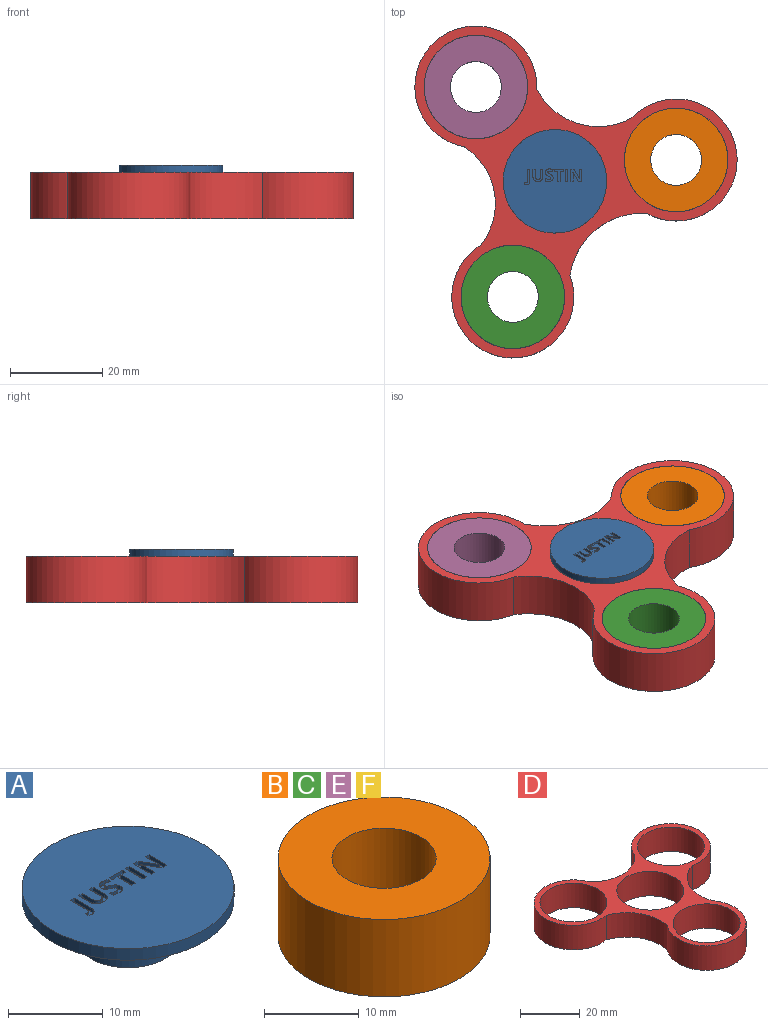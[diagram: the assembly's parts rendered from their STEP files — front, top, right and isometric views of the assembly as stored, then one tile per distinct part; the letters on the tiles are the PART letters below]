
ASSEMBLY  parts=6 mates=5
PART A: 90 faces, bbox 22.4x22.4x6.5 mm
  f0: plane 22.4x22.4mm, normal (0,0,1), area 378.7mm2, adj f3,f5,f6,f7,f8,f9,f10,f11
  f1: cylinder r=5.5mm len=11mm, axis (0,0,-1), area 172.8mm2, adj f2,f4
  f2: plane 11x11mm, normal (0,0,-1), area 95mm2, adj f1
  f3: cylinder r=11.2mm len=22.4mm, axis (0,0,-1), area 105.6mm2, adj f0,f4
  f4: plane 22.4x22.4mm, normal (0,0,-1), area 299mm2, adj f1,f3
  f5: plane 0.71x0.5mm, normal (0,1,0), area 0.4mm2, adj f0,f6,f18,f19
  f6: plane 2.63x0.5mm, normal (-1,0,0), area 1.3mm2, adj f0,f5,f7,f19
  f7: plane 0.5x0.5mm, normal (0,-1,0), area 0.3mm2, adj f0,f6,f8,f19
  f8: plane 1.25x0.5mm, normal (1,0,0), area 0.6mm2, adj f0,f7,f9,f19
  f9: extruded ~0.73x0.5mm, area 0.4mm2, adj f0,f8,f10,f19
  f10: plane 0.5x0.01mm, normal (0,-1,0), area 0mm2, adj f0,f9,f11,f19
  f11: plane 1.97x1.14mm, normal (-0.87,-0.5,0), area 1.1mm2, adj f0,f10,f12,f19
  f12: plane 0.7x0.5mm, normal (0,-1,0), area 0.4mm2, adj f0,f11,f13,f19
  f13: plane 2.63x0.5mm, normal (1,0,0), area 1.3mm2, adj f0,f12,f14,f19
  f14: plane 0.5x0.5mm, normal (0,1,0), area 0.2mm2, adj f0,f13,f15,f19
  f15: plane 1.24x0.5mm, normal (-1,0,0), area 0.6mm2, adj f0,f14,f16,f19
  f16: extruded ~0.75x0.5mm, area 0.4mm2, adj f0,f15,f17,f19
  f17: plane 0.5x0.02mm, normal (0,1,0), area 0mm2, adj f0,f16,f18,f19
  f18: plane 1.99x1.15mm, normal (0.87,0.5,0), area 1.1mm2, adj f0,f5,f17,f19
  f19: plane 2.63x2.34mm, normal (0,0,1), area 3.9mm2, adj f5,f6,f7,f8,f9,f10,f11,f12
  f20: plane 2.63x0.5mm, normal (1,0,0), area 1.3mm2, adj f0,f21,f23,f24
  f21: plane 0.56x0.5mm, normal (0,1,0), area 0.3mm2, adj f0,f20,f22,f24
  f22: plane 2.63x0.5mm, normal (-1,0,0), area 1.3mm2, adj f0,f21,f23,f24
  f23: plane 0.56x0.5mm, normal (0,-1,0), area 0.3mm2, adj f0,f20,f22,f24
  f24: plane 2.63x0.56mm, normal (0,0,1), area 1.5mm2, adj f20,f21,f22,f23
  f25: plane 0.56x0.5mm, normal (0,1,0), area 0.3mm2, adj f0,f26,f32,f33
  f26: plane 2.17x0.5mm, normal (-1,0,0), area 1.1mm2, adj f0,f25,f27,f33
  f27: plane 0.71x0.5mm, normal (0,1,0), area 0.4mm2, adj f0,f26,f28,f33
  f28: plane 0.5x0.46mm, normal (-1,0,0), area 0.2mm2, adj f0,f27,f29,f33
  f29: plane 1.99x0.5mm, normal (0,-1,0), area 1mm2, adj f0,f28,f30,f33
  f30: plane 0.5x0.46mm, normal (1,0,0), area 0.2mm2, adj f0,f29,f31,f33
  f31: plane 0.72x0.5mm, normal (0,1,0), area 0.4mm2, adj f0,f30,f32,f33
  f32: plane 2.17x0.5mm, normal (1,0,0), area 1.1mm2, adj f0,f25,f31,f33
  f33: plane 2.63x1.99mm, normal (0,0,1), area 2.1mm2, adj f25,f26,f27,f28,f29,f30,f31,f32
  f34: extruded ~0.56x0.5mm, area 0.3mm2, adj f0,f35,f61,f62
  f35: extruded ~0.5x0.43mm, area 0.2mm2, adj f0,f34,f36,f62
  f36: extruded ~0.51x0.5mm, area 0.3mm2, adj f0,f35,f37,f62
  f37: extruded ~0.5x0.35mm, area 0.2mm2, adj f0,f36,f38,f62
  f38: extruded ~0.5x0.11mm, area 0.1mm2, adj f0,f37,f39,f62
  f39: extruded ~0.5x0.13mm, area 0.1mm2, adj f0,f38,f40,f62
  f40: extruded ~0.5x0.19mm, area 0.1mm2, adj f0,f39,f41,f62
  f41: extruded ~0.5x0.24mm, area 0.1mm2, adj f0,f40,f42,f62
  f42: extruded ~0.5x0.27mm, area 0.1mm2, adj f0,f41,f43,f62
  f43: extruded ~0.5x0.35mm, area 0.2mm2, adj f0,f42,f44,f62
  f44: plane 0.5x0.43mm, normal (-0.92,0.38,0), area 0.2mm2, adj f0,f43,f45,f62
  f45: extruded ~0.5x0.39mm, area 0.2mm2, adj f0,f44,f46,f62
  f46: extruded ~0.5x0.39mm, area 0.2mm2, adj f0,f45,f47,f62
  f47: extruded ~0.65x0.5mm, area 0.3mm2, adj f0,f46,f48,f62
  f48: extruded ~0.55x0.5mm, area 0.3mm2, adj f0,f47,f49,f62
  f49: extruded ~0.5x0.32mm, area 0.2mm2, adj f0,f48,f50,f62
  f50: extruded ~0.5x0.24mm, area 0.2mm2, adj f0,f49,f51,f62
  f51: extruded ~0.5x0.36mm, area 0.2mm2, adj f0,f50,f52,f62
  f52: extruded ~0.5x0.34mm, area 0.2mm2, adj f0,f51,f53,f62
  f53: extruded ~0.5x0.13mm, area 0.1mm2, adj f0,f52,f54,f62
  f54: extruded ~0.5x0.14mm, area 0.1mm2, adj f0,f53,f55,f62
  f55: extruded ~0.5x0.21mm, area 0.1mm2, adj f0,f54,f56,f62
  f56: extruded ~0.5x0.28mm, area 0.1mm2, adj f0,f55,f57,f62
  f57: extruded ~0.5x0.34mm, area 0.2mm2, adj f0,f56,f58,f62
  f58: extruded ~0.5x0.45mm, area 0.2mm2, adj f0,f57,f59,f62
  f59: plane 0.52x0.5mm, normal (1,0,0), area 0.3mm2, adj f0,f58,f60,f62
  f60: extruded ~0.75x0.5mm, area 0.4mm2, adj f0,f59,f61,f62
  f61: extruded ~0.71x0.5mm, area 0.4mm2, adj f0,f34,f60,f62
  f62: plane 2.71x1.72mm, normal (0,0,1), area 2.6mm2, adj f34,f35,f36,f37,f38,f39,f40,f41
  f63: plane 1.7x0.5mm, normal (-1,0,0), area 0.9mm2, adj f0,f64,f77,f78
  f64: plane 0.56x0.5mm, normal (0,-1,0), area 0.3mm2, adj f0,f63,f65,f78
  f65: plane 1.61x0.5mm, normal (1,0,0), area 0.8mm2, adj f0,f64,f66,f78
  f66: extruded ~0.5x0.45mm, area 0.2mm2, adj f0,f65,f67,f78
  f67: extruded ~0.5x0.4mm, area 0.2mm2, adj f0,f66,f68,f78
  f68: extruded ~0.5x0.41mm, area 0.2mm2, adj f0,f67,f69,f78
  f69: extruded ~0.5x0.45mm, area 0.2mm2, adj f0,f68,f70,f78
  f70: plane 1.61x0.5mm, normal (-1,0,0), area 0.8mm2, adj f0,f69,f71,f78
  f71: plane 0.56x0.5mm, normal (0,-1,0), area 0.3mm2, adj f0,f70,f72,f78
  f72: plane 1.7x0.5mm, normal (1,0,0), area 0.8mm2, adj f0,f71,f73,f78
  f73: extruded ~0.71x0.5mm, area 0.4mm2, adj f0,f72,f74,f78
  f74: extruded ~0.79x0.5mm, area 0.4mm2, adj f0,f73,f75,f78
  f75: extruded ~0.58x0.5mm, area 0.3mm2, adj f0,f74,f76,f78
  f76: extruded ~0.5x0.38mm, area 0.3mm2, adj f0,f75,f77,f78
  f77: extruded ~0.51x0.5mm, area 0.3mm2, adj f0,f63,f76,f78
  f78: plane 2.67x2.16mm, normal (0,0,1), area 3.2mm2, adj f63,f64,f65,f66,f67,f68,f69,f70
  f79: extruded ~0.5x0.33mm, area 0.2mm2, adj f0,f80,f88,f89
  f80: extruded ~0.62x0.5mm, area 0.3mm2, adj f0,f79,f81,f89
  f81: extruded ~0.7x0.5mm, area 0.4mm2, adj f0,f80,f82,f89
  f82: plane 2.46x0.5mm, normal (-1,0,0), area 1.2mm2, adj f0,f81,f83,f89
  f83: plane 0.56x0.5mm, normal (0,-1,0), area 0.3mm2, adj f0,f82,f84,f89
  f84: plane 2.47x0.5mm, normal (1,0,0), area 1.2mm2, adj f0,f83,f85,f89
  f85: extruded ~0.5x0.36mm, area 0.2mm2, adj f0,f84,f86,f89
  f86: extruded ~0.5x0.26mm, area 0.1mm2, adj f0,f85,f87,f89
  f87: extruded ~0.5x0.26mm, area 0.1mm2, adj f0,f86,f88,f89
  f88: plane 0.5x0.46mm, normal (1,0,0), area 0.2mm2, adj f0,f79,f87,f89
  f89: plane 3.41x1.16mm, normal (0,0,1), area 2.1mm2, adj f79,f80,f81,f82,f83,f84,f85,f86
PART B: 4 faces, bbox 22.4x22.4x10 mm
  f0: cylinder r=5.5mm len=11mm, axis (0,0,-1), area 345.6mm2, adj f2,f3
  f1: cylinder r=11.2mm len=22.4mm, axis (0,0,-1), area 703.7mm2, adj f2,f3
  f2: plane 22.4x22.4mm, normal (0,0,1), area 299mm2, adj f0,f1
  f3: plane 22.4x22.4mm, normal (0,0,-1), area 299mm2, adj f0,f1
PART C: same geometry as B
PART D: 12 faces, bbox 72.5x66.3x10 mm
  f0: cylinder r=13.2mm len=26.4mm, axis (0,0,-1), area 588.4mm2, adj f1,f7,f10,f11
  f1: cylinder r=15.02mm len=19.19mm, axis (0,0,-1), area 238.8mm2, adj f0,f2,f10,f11
  f2: cylinder r=13.2mm len=26.4mm, axis (0,0,-1), area 602.6mm2, adj f1,f3,f10,f11
  f3: cylinder r=14.48mm len=21.47mm, axis (0,0,-1), area 241.8mm2, adj f2,f4,f10,f11
  f4: cylinder r=13.2mm len=26.4mm, axis (0,0,-1), area 597.4mm2, adj f3,f7,f10,f11
  f5: cylinder r=11.2mm len=22.4mm, axis (0,0,-1), area 703.7mm2, adj f10,f11
  f6: cylinder r=11.2mm len=22.4mm, axis (0,0,-1), area 703.7mm2, adj f10,f11
  f7: cylinder r=15.79mm len=18.63mm, axis (0,0,-1), area 233.9mm2, adj f0,f4,f10,f11
  f8: cylinder r=11.2mm len=22.4mm, axis (0,0,-1), area 703.7mm2, adj f10,f11
  f9: cylinder r=11.2mm len=22.4mm, axis (0,0,-1), area 703.7mm2, adj f10,f11
  f10: plane 72.49x66.31mm, normal (0,0,1), area 796.1mm2, adj f0,f1,f2,f3,f4,f5,f6,f7
  f11: plane 72.49x66.31mm, normal (0,0,-1), area 796.1mm2, adj f0,f1,f2,f3,f4,f5,f6,f7
PART E: same geometry as B
PART F: same geometry as B
PLACE A t=(-17.6,-8.86,1.96)mm
PLACE B rot(axis=(0,0,1),10deg) t=(8.6,-4.24,-3.04)mm
PLACE C rot(axis=(0,0,1),10deg) t=(-26.71,-33.86,-3.04)mm
PLACE D rot(axis=(0,0,1),100deg) t=(-17.6,-8.86,-3.04)mm
PLACE E rot(axis=(0,0,1),10deg) t=(-34.7,11.53,-3.04)mm
PLACE F t=(-17.6,-8.86,-3.04)mm fixed
MATE fastened D.f4 <-> C.f0  axis (0,0,-1) through (-26.71,-33.86,6.96)mm
MATE revolute D.f9 <-> F.f0  axis (0,0,-1) through (-17.6,-8.86,6.96)mm
MATE fastened E.f0 <-> D.f2  axis (0,0,-1) through (-34.7,11.53,6.96)mm
MATE fastened F.f1 <-> A.f3  axis (0,0,1) through (-17.6,-8.86,6.96)mm
MATE fastened B.f1 <-> D.f8  axis (0,0,1) through (8.6,-4.24,6.96)mm
